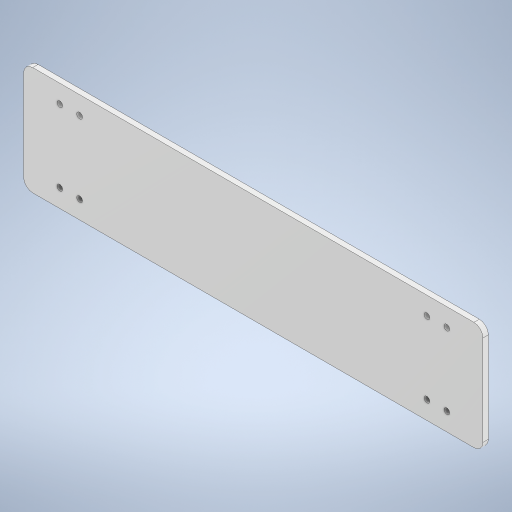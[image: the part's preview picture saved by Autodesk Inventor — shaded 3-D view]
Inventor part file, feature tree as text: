
AUTODESK INVENTOR PART (.ipt)
format: ipt  version: 2024.3 (Build 283343000, 343)  size: 285,696 bytes
history: native  units: mm
features: sketch x4, extrude x3, other x1, fillet x1, hole x1
ambient origin geometry x8: Origin, YZ Plane, XZ Plane, XY Plane, X Axis, Y Axis, Z Axis, Center Point
bodies: Body1 (feature_tree)
feature tree (10):
  other  "ソリッド1"
  extrude  "押し出し1"  Depth=260.0mm
  extrude  "押し出し4"  Depth=3.0mm
  extrude  "押し出し7"  Depth=60.0mm TaperAngle=0.0deg
  fillet  "フィレット1"  Radius=3.0mm
  hole  "穴1"  [1 undecoded]
  sketch  "スケッチ1"
  sketch  "スケッチ5"
  sketch  "スケッチ8"
  sketch  "スケッチ13"
note: 1 required parameter value undecoded (feature->parameter linkage not recoverable at this tier; creation-order binding heuristic only, values carry confidence <= 0.55)
